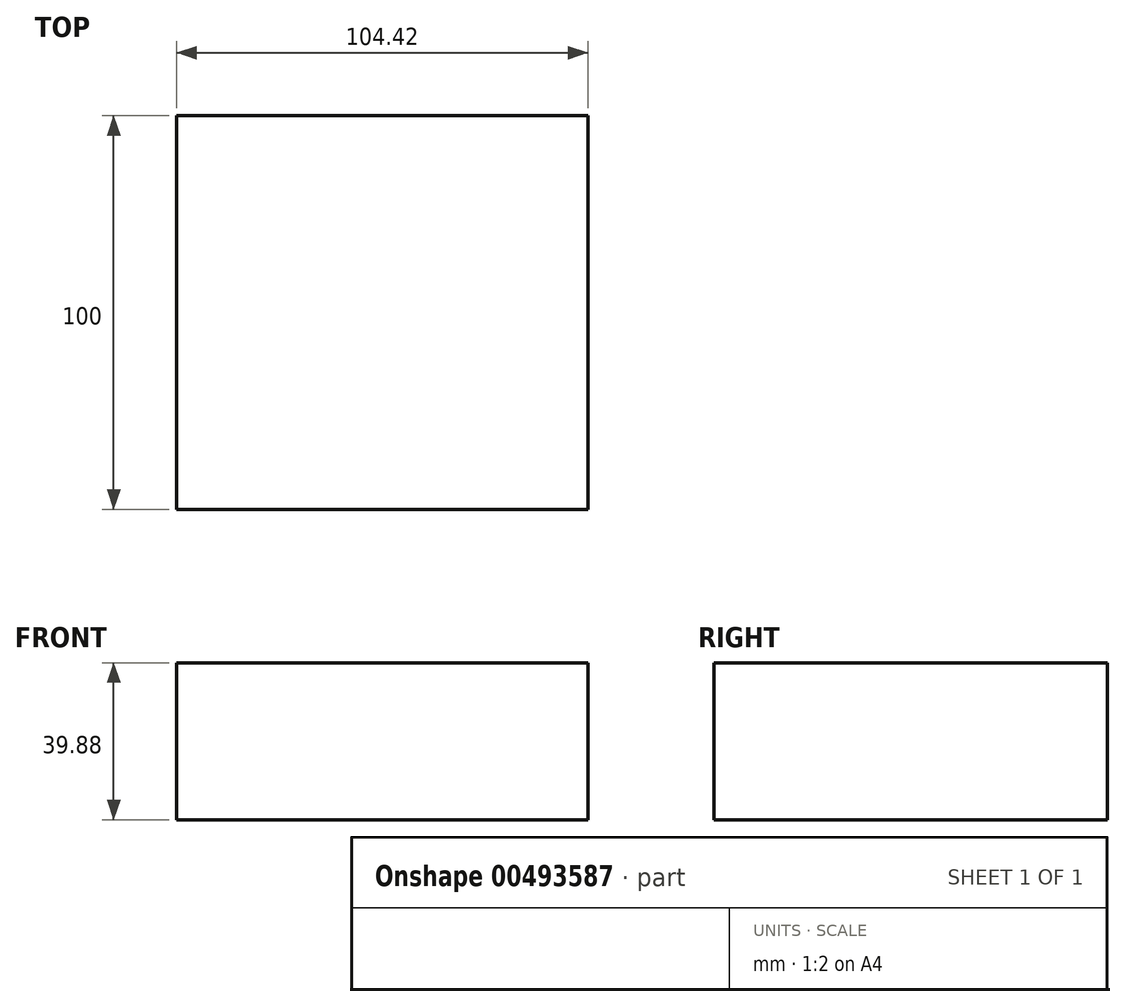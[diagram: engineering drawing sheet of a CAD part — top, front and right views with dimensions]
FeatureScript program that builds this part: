
annotation { "Feature Type Name" : "Feature", "Feature Type Description" : "" }
export const myFeature = defineFeature(function(context is Context, id is Id, definition is map)
    precondition{}
    {
        {
            var Q0;
            Q0=qCreatedBy(makeId("Front.planeOp"),FACE);
            var sketch = newSketch(context, id + "F0", { "sketchPlane" : qUnion([Q0])});
            skLineSegment(sketch, "E0.bottom", {"start": v(-52.21, -19.94) * mm, "end": v(52.21, -19.94) * mm});
            skLineSegment(sketch, "E0.top", {"start": v(-52.21, 19.94) * mm, "end": v(52.21, 19.94) * mm});
            skLineSegment(sketch, "E0.left", {"start": v(-52.21, -19.94) * mm, "end": v(-52.21, 19.94) * mm});
            skLineSegment(sketch, "E0.right", {"start": v(52.21, -19.94) * mm, "end": v(52.21, 19.94) * mm});
            skPoint(sketch, "E0.middle", {"position": v(0, 0) * mm});
            skSolve(sketch);
        }
        {
            var Q0;
            Q0=makeQuery(id+"F0.imprint","IMPRINT",FACE,{"disambiguationData":[TD([[makeQuery(id+"F0.imprint","IMPRINT",EDGE,{"derivedFrom":sQuery(id+"F0.wireOp",EDGE,"E0.bottom")}),1.0]])]});
            extrude(context, id + "F1", {"entities" : qUnion([Q0]), "endBound" : BoundingType.SYMMETRIC, "depth" : 100 * mm});
        }
    });
